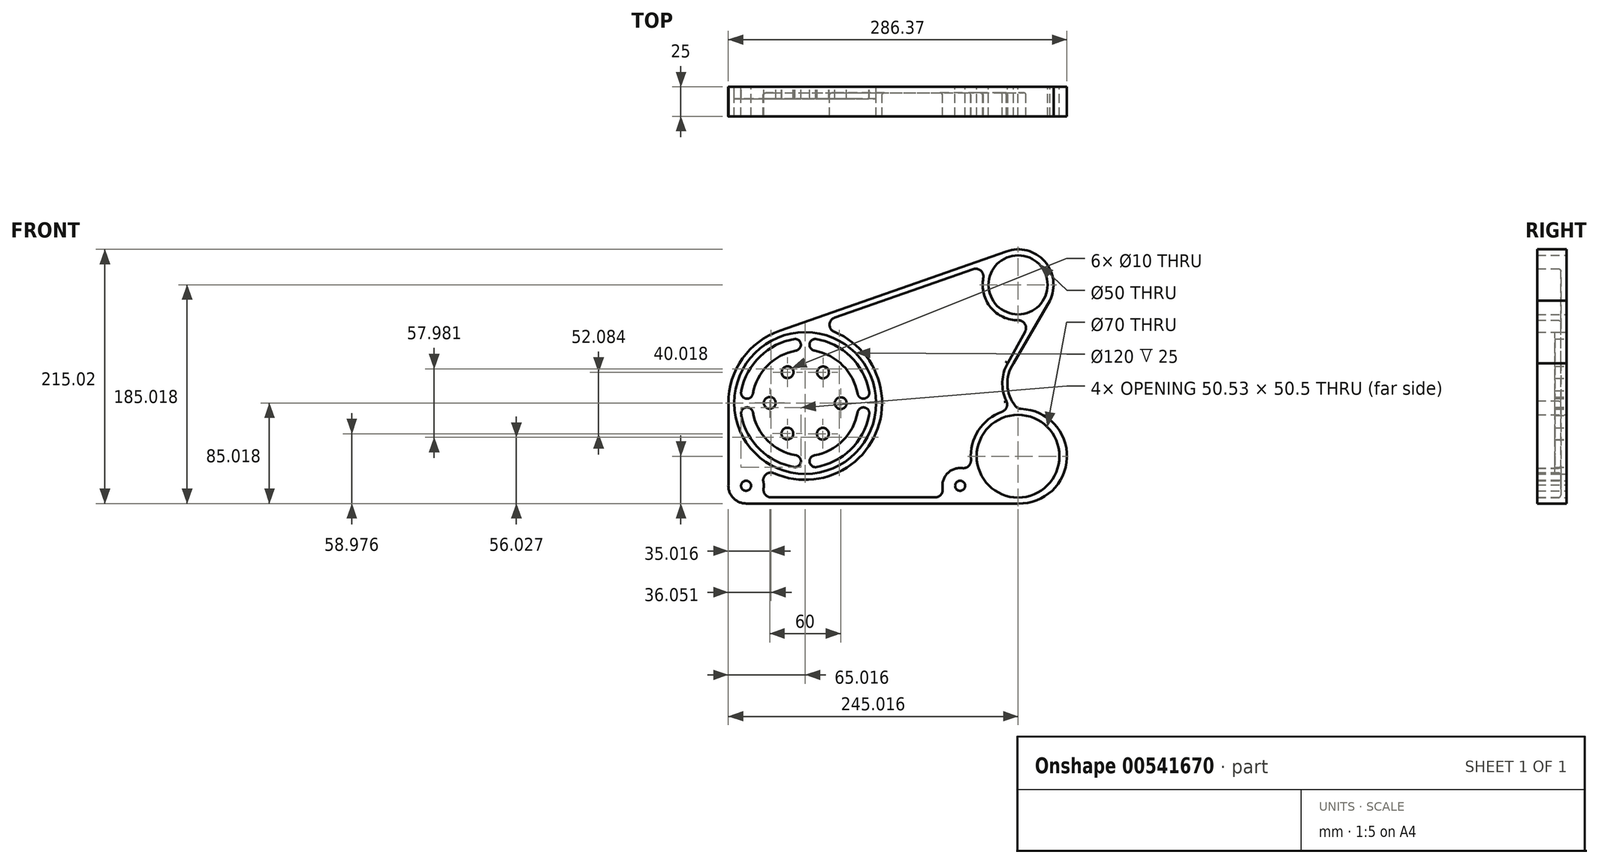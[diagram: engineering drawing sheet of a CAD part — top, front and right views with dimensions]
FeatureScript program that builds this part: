
annotation { "Feature Type Name" : "Feature", "Feature Type Description" : "" }
export const myFeature = defineFeature(function(context is Context, id is Id, definition is map)
    precondition{}
    {
        {
            var Q0;
            Q0=qCreatedBy(makeId("Front.planeOp"),FACE);
            var sketch = newSketch(context, id + "F0", { "sketchPlane" : qUnion([Q0])});
            skCircle(sketch, "E0", {"center": v(-308, 188.88) * mm, "radius": 60 * mm});
            skCircle(sketch, "E1", {"center": v(-278, 188.76) * mm, "radius": 5 * mm});
            skCircle(sketch, "E2.1.0", {"center": v(-292.9, 214.8) * mm, "radius": 5 * mm});
            skCircle(sketch, "E2.2.0", {"center": v(-322.9, 214.92) * mm, "radius": 5 * mm});
            skCircle(sketch, "E2.3.0", {"center": v(-338, 189) * mm, "radius": 5 * mm});
            skCircle(sketch, "E2.4.0", {"center": v(-323.1, 162.96) * mm, "radius": 5 * mm});
            skCircle(sketch, "E2.5.0", {"center": v(-293.1, 162.84) * mm, "radius": 5 * mm});
            skLineSegment(sketch, "E3", {"start": v(-442.41, 188.88) * mm, "end": v(134.88, 188.88) * mm, "construction": true});
            skCircle(sketch, "E4", {"center": v(-358, 118.88) * mm, "radius": 4.25 * mm});
            skCircle(sketch, "E5", {"center": v(-177, 118.88) * mm, "radius": 4.25 * mm});
            skCircle(sketch, "E6", {"center": v(-128, 143.88) * mm, "radius": 35 * mm});
            skCircle(sketch, "E7", {"center": v(-128, 288.88) * mm, "radius": 25 * mm});
            skArc(sketch, "E8.0", {"start": v(-101.14, 275.52) * mm, "mid": v(-105.5, 308.72) * mm, "end": v(-137.9, 317.2) * mm});
            skArc(sketch, "E9.0", {"start": v(-329.45, 250.24) * mm, "mid": v(-361, 226.5) * mm, "end": v(-373, 188.88) * mm});
            skLineSegment(sketch, "E10", {"start": v(-358, 103.88) * mm, "end": v(-128, 103.88) * mm});
            skLineSegment(sketch, "E11", {"start": v(-373, 188.88) * mm, "end": v(-373, 119.57) * mm});
            skLineSegment(sketch, "E12", {"start": v(-329.45, 250.24) * mm, "end": v(-137.9, 317.2) * mm});
            skLineSegment(sketch, "E13.0", {"start": v(-283.03, 261.17) * mm, "end": v(-165.96, 302.1) * mm});
            skArc(sketch, "E14", {"start": v(-131.85, 222.34) * mm, "mid": v(-137.04, 204.02) * mm, "end": v(-130.16, 186.26) * mm});
            skArc(sketch, "E15.0", {"start": v(-141.55, 181.52) * mm, "mid": v(-161.6, 165.57) * mm, "end": v(-167.88, 140.73) * mm});
            skLineSegment(sketch, "E16", {"start": v(-136.67, 222.67) * mm, "end": v(-122.08, 249.25) * mm});
            skLineSegment(sketch, "E17.trimOffspring", {"start": v(-131.85, 222.34) * mm, "end": v(-101.14, 275.52) * mm});
            skArc(sketch, "E18.trimOffspring", {"start": v(-157.43, 294.7) * mm, "mid": v(-151.12, 269.76) * mm, "end": v(-127.82, 258.88) * mm});
            skArc(sketch, "E19", {"start": v(-175.16, 133.77) * mm, "mid": v(-187.78, 129.3) * mm, "end": v(-191.8, 116.52) * mm});
            skArc(sketch, "E20.trimOffspring", {"start": v(-128, 103.88) * mm, "mid": v(-86.67, 142.58) * mm, "end": v(-125.37, 183.91) * mm});
            skLineSegment(sketch, "E21.trimOffspring", {"start": v(-336.79, 109) * mm, "end": v(-198.23, 109) * mm});
            skArc(sketch, "E22", {"start": v(-373, 119.57) * mm, "mid": v(-368.86, 108.51) * mm, "end": v(-358, 103.88) * mm});
            skArc(sketch, "E23", {"start": v(-283.03, 261.17) * mm, "mid": v(-287.38, 255.2) * mm, "end": v(-283.35, 249.02) * mm});
            skArc(sketch, "E24", {"start": v(-157.43, 294.7) * mm, "mid": v(-159.55, 300.87) * mm, "end": v(-165.96, 302.1) * mm});
            skArc(sketch, "E25", {"start": v(-122.08, 249.25) * mm, "mid": v(-122.2, 255.7) * mm, "end": v(-127.82, 258.88) * mm});
            skArc(sketch, "E26", {"start": v(-141.55, 181.52) * mm, "mid": v(-137.7, 185.25) * mm, "end": v(-137.97, 190.6) * mm});
            skArc(sketch, "E27", {"start": v(-130.16, 186.26) * mm, "mid": v(-128.02, 184.57) * mm, "end": v(-125.37, 183.91) * mm});
            skArc(sketch, "E28", {"start": v(-175.16, 133.77) * mm, "mid": v(-169.87, 135.52) * mm, "end": v(-167.88, 140.73) * mm});
            skArc(sketch, "E29", {"start": v(-198.23, 109) * mm, "mid": v(-193.28, 111.28) * mm, "end": v(-191.8, 116.52) * mm});
            skArc(sketch, "E30", {"start": v(-136.67, 222.67) * mm, "mid": v(-141.3, 206.8) * mm, "end": v(-137.96, 190.6) * mm});
            skArc(sketch, "E31", {"start": v(-334.4, 129.48) * mm, "mid": v(-341.15, 128.57) * mm, "end": v(-343.38, 122.13) * mm});
            skArc(sketch, "E32", {"start": v(-343.2, 116.52) * mm, "mid": v(-341.73, 111.28) * mm, "end": v(-336.79, 109) * mm});
            skArc(sketch, "E33.trimOffspring", {"start": v(-334.4, 129.48) * mm, "mid": v(-248.23, 163.35) * mm, "end": v(-283.35, 249.02) * mm});
            skArc(sketch, "E34.trimOffspring", {"start": v(-343.2, 116.52) * mm, "mid": v(-343.03, 119.33) * mm, "end": v(-343.38, 122.13) * mm});
            skArc(sketch, "E35", {"start": v(-299.32, 243.12) * mm, "mid": v(-304.3, 238.55) * mm, "end": v(-300.19, 233.2) * mm});
            skArc(sketch, "E36", {"start": v(-263.69, 196.7) * mm, "mid": v(-257.47, 192.73) * mm, "end": v(-254.06, 199.27) * mm});
            skArc(sketch, "E37", {"start": v(-300.19, 233.2) * mm, "mid": v(-276.18, 220.7) * mm, "end": v(-263.69, 196.7) * mm});
            skPoint(sketch, "E38.orphan", {"position": v(-299.32, 243.12) * mm});
            skArc(sketch, "E39", {"start": v(-299.32, 243.12) * mm, "mid": v(-269.78, 228.33) * mm, "end": v(-254.06, 199.27) * mm});
            skArc(sketch, "E40.MirrorCS", {"start": v(-352.32, 196.7) * mm, "mid": v(-358.54, 192.73) * mm, "end": v(-361.94, 199.27) * mm});
            skArc(sketch, "E41.MirrorCS", {"start": v(-316.69, 243.12) * mm, "mid": v(-346.23, 228.33) * mm, "end": v(-361.94, 199.27) * mm});
            skArc(sketch, "E42.MirrorCS", {"start": v(-316.69, 243.12) * mm, "mid": v(-311.7, 238.55) * mm, "end": v(-315.82, 233.2) * mm});
            skArc(sketch, "E43.MirrorCS", {"start": v(-315.82, 233.2) * mm, "mid": v(-339.82, 220.7) * mm, "end": v(-352.32, 196.7) * mm});
            skArc(sketch, "E44.MirrorCS", {"start": v(-263.69, 181.06) * mm, "mid": v(-257.47, 185.03) * mm, "end": v(-254.06, 178.49) * mm});
            skArc(sketch, "E45.MirrorCS", {"start": v(-300.19, 144.56) * mm, "mid": v(-276.18, 157.06) * mm, "end": v(-263.69, 181.06) * mm});
            skArc(sketch, "E46.MirrorCS", {"start": v(-299.32, 134.64) * mm, "mid": v(-269.78, 149.43) * mm, "end": v(-254.06, 178.49) * mm});
            skArc(sketch, "E47.MirrorCS", {"start": v(-299.32, 134.64) * mm, "mid": v(-304.3, 139.2) * mm, "end": v(-300.19, 144.56) * mm});
            skArc(sketch, "E48.MirrorCS", {"start": v(-316.69, 134.64) * mm, "mid": v(-311.7, 139.2) * mm, "end": v(-315.82, 144.56) * mm});
            skArc(sketch, "E49.MirrorCS", {"start": v(-316.69, 134.64) * mm, "mid": v(-346.23, 149.43) * mm, "end": v(-361.94, 178.49) * mm});
            skArc(sketch, "E50.MirrorCS", {"start": v(-315.82, 144.56) * mm, "mid": v(-339.82, 157.06) * mm, "end": v(-352.32, 181.06) * mm});
            skArc(sketch, "E51.MirrorCS", {"start": v(-352.32, 181.06) * mm, "mid": v(-358.54, 185.03) * mm, "end": v(-361.94, 178.49) * mm});
            skSolve(sketch);
        }
        {
            var Q0;
            Q0=makeQuery(id+"F0.imprint","IMPRINT",FACE,{"disambiguationData":[TD([[makeQuery(id+"F0.imprint","IMPRINT",EDGE,{"derivedFrom":sQuery(id+"F0.wireOp",EDGE,"E0")}),1.0]])]});
            extrude(context, id + "F1", {"entities" : qUnion([Q0]), "depth" : 10 * mm, "offsetDistance" : 25 * mm});
        }
        {
            var Q0;
            Q0=makeQuery(id+"F0.imprint","IMPRINT",FACE,{"disambiguationData":[TD([[makeQuery(id+"F0.imprint","IMPRINT",EDGE,{"derivedFrom":sQuery(id+"F0.wireOp",EDGE,"E0")}),-1.0]])]});
            extrude(context, id + "F2", {"entities" : qUnion([Q0]), "depth" : 25 * mm, "offsetDistance" : 25 * mm});
        }
        {
            var Q0;
            Q0=makeQuery(id+"F0.imprint","IMPRINT",FACE,{"disambiguationData":[TD([[makeQuery(id+"F0.imprint","IMPRINT",EDGE,{"derivedFrom":sQuery(id+"F0.wireOp",EDGE,"E13.0")}),-1.0]])]});
            extrude(context, id + "F3", {"entities" : qUnion([Q0]), "operationType" : NewBodyOperationType.ADD, "depth" : 5 * mm, "offsetDistance" : 25 * mm});
        }
        {
            var Q0;
            Q0=makeQuery(id+"F3.opExtrude","CAP_FACE",FACE,{"disambiguationData":[OSD([sQuery(id+"F0.wireOp",EDGE,"E13.0"),sQuery(id+"F0.wireOp",EDGE,"E15.0"),sQuery(id+"F0.wireOp",EDGE,"E16"),sQuery(id+"F0.wireOp",EDGE,"E18.trimOffspring"),sQuery(id+"F0.wireOp",EDGE,"E19"),sQuery(id+"F0.wireOp",EDGE,"E21.trimOffspring"),sQuery(id+"F0.wireOp",EDGE,"E23"),sQuery(id+"F0.wireOp",EDGE,"E24"),sQuery(id+"F0.wireOp",EDGE,"E25"),sQuery(id+"F0.wireOp",EDGE,"E26"),sQuery(id+"F0.wireOp",EDGE,"E28"),sQuery(id+"F0.wireOp",EDGE,"E29"),sQuery(id+"F0.wireOp",EDGE,"E30"),sQuery(id+"F0.wireOp",EDGE,"E31"),sQuery(id+"F0.wireOp",EDGE,"E32"),sQuery(id+"F0.wireOp",EDGE,"E33.trimOffspring"),sQuery(id+"F0.wireOp",EDGE,"E34.trimOffspring")])],"isStart":false});
            fillet(context, id + "F4", {"entities" : qUnion([Q0]), "radius" : 2 * mm, "tangentPropagation" : true, "allowEdgeOverflow" : false});
        }
    });
